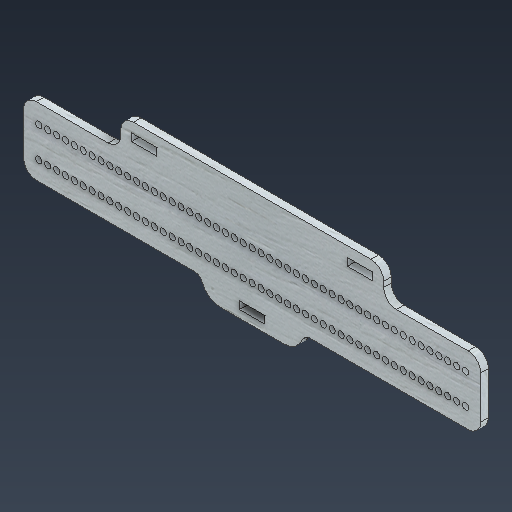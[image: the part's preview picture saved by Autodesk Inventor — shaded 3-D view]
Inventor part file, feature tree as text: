
AUTODESK INVENTOR PART (.ipt)
format: ipt  version: 2025.3 (Build 293356000, 356)  size: 411,136 bytes
history: native  units: mm
features: sketch x3, other x2, extrude x1
ambient origin geometry x8: Origin, YZ Plane, XZ Plane, XY Plane, X Axis, Y Axis, Z Axis, Center Point
bodies: Body1 (feature_tree)
feature tree (6):
  other  "實體1"
  extrude  "擠出1"  Depth=10.0mm
  sketch  "草圖3"
  sketch  "草圖5"
  sketch  "草圖1"
  other  "草圖 - 矩形陣列5"
